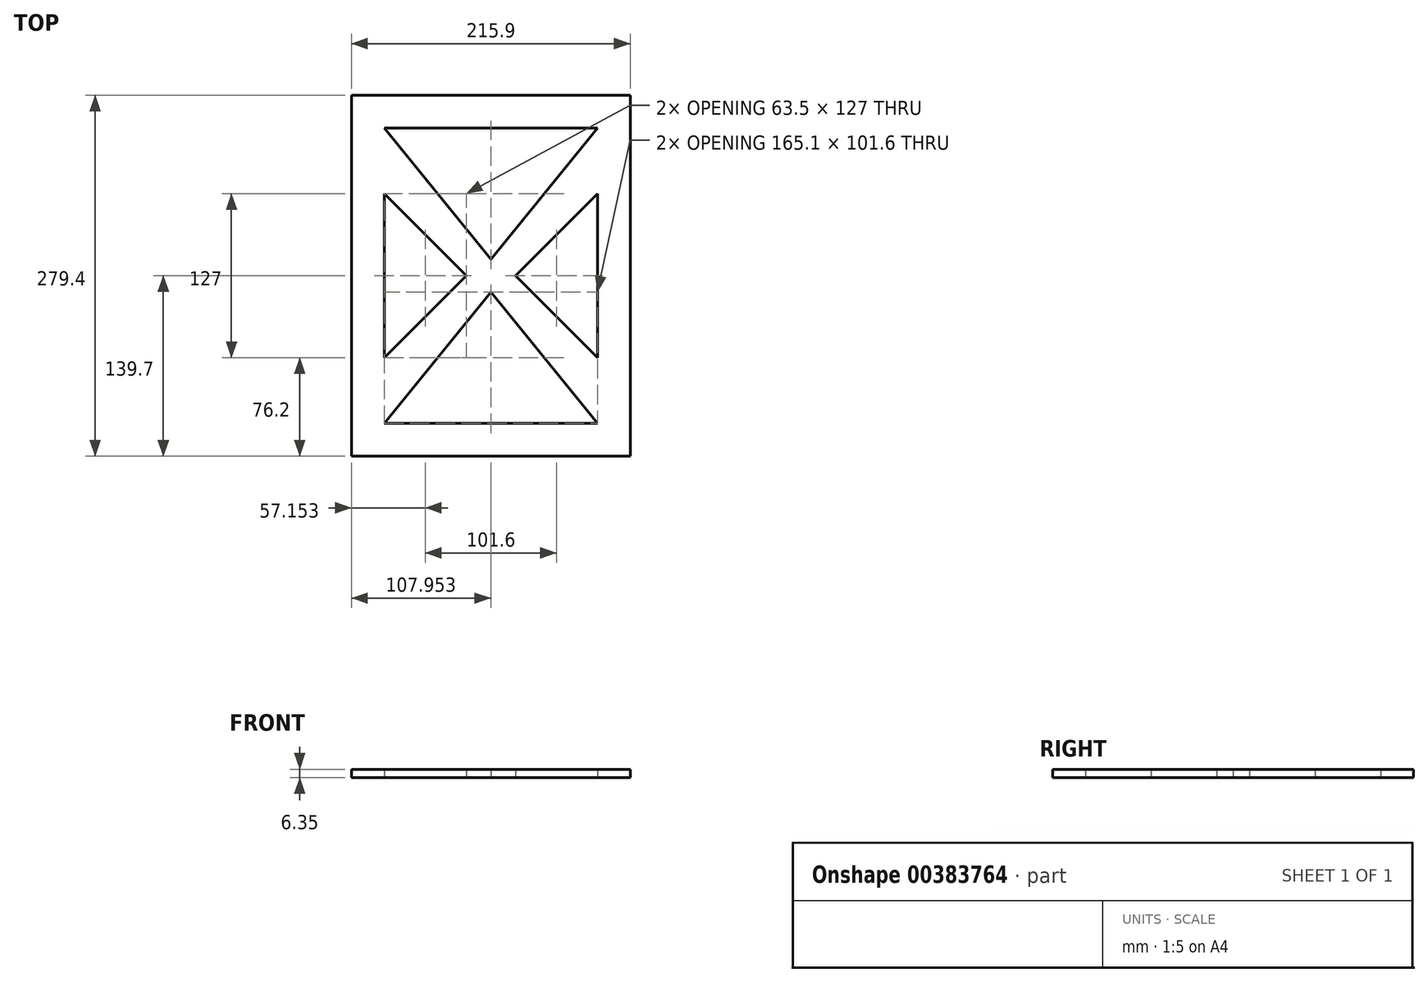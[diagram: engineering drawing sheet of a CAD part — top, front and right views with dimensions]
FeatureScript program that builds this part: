
annotation { "Feature Type Name" : "Feature", "Feature Type Description" : "" }
export const myFeature = defineFeature(function(context is Context, id is Id, definition is map)
    precondition{}
    {
        {
            var Q0;
            Q0=qCreatedBy(makeId("Top.planeOp"),FACE);
            var sketch = newSketch(context, id + "F0", { "sketchPlane" : qUnion([Q0])});
            skLineSegment(sketch, "E0.bottom", {"start": v(4.75, 0) * mm, "end": v(220.65, 0) * mm});
            skLineSegment(sketch, "E0.top", {"start": v(4.75, 279.4) * mm, "end": v(220.65, 279.4) * mm});
            skLineSegment(sketch, "E0.left", {"start": v(4.75, 0) * mm, "end": v(4.75, 279.4) * mm});
            skLineSegment(sketch, "E0.right", {"start": v(220.65, 0) * mm, "end": v(220.65, 279.4) * mm});
            skLineSegment(sketch, "E1.0", {"start": v(30.15, 254) * mm, "end": v(195.25, 254) * mm});
            skLineSegment(sketch, "E2", {"start": v(112.7, 152.4) * mm, "end": v(195.25, 254) * mm});
            skLineSegment(sketch, "E3", {"start": v(112.7, 152.4) * mm, "end": v(30.15, 254) * mm});
            skPoint(sketch, "E4.endSnap0", {"position": v(220.65, 139.7) * mm});
            skLineSegment(sketch, "E5.MirrorCS", {"start": v(112.7, 127) * mm, "end": v(195.25, 25.4) * mm});
            skLineSegment(sketch, "E6.MirrorCS", {"start": v(112.7, 127) * mm, "end": v(30.15, 25.4) * mm});
            skLineSegment(sketch, "E7.MirrorCS", {"start": v(30.15, 25.4) * mm, "end": v(195.25, 25.4) * mm});
            skLineSegment(sketch, "E8", {"start": v(30.15, 203.2) * mm, "end": v(93.65, 139.7) * mm});
            skLineSegment(sketch, "E9", {"start": v(93.65, 139.7) * mm, "end": v(30.15, 76.2) * mm});
            skLineSegment(sketch, "E10.trimOffspring", {"start": v(30.15, 76.2) * mm, "end": v(30.15, 203.2) * mm});
            skLineSegment(sketch, "E11.MirrorCS", {"start": v(131.75, 139.7) * mm, "end": v(195.25, 76.2) * mm});
            skLineSegment(sketch, "E12.MirrorCS", {"start": v(195.25, 76.2) * mm, "end": v(195.25, 203.2) * mm});
            skLineSegment(sketch, "E13.MirrorCS", {"start": v(195.25, 203.2) * mm, "end": v(131.75, 139.7) * mm});
            skSolve(sketch);
        }
        {
            var Q0;
            Q0=makeQuery(id+"F0.imprint","IMPRINT",FACE,{"disambiguationData":[TD([[makeQuery(id+"F0.imprint","IMPRINT",EDGE,{"derivedFrom":sQuery(id+"F0.wireOp",EDGE,"E0.bottom")}),1.0]])]});
            extrude(context, id + "F1", {"entities" : qUnion([Q0]), "depth" : 6.35 * mm});
        }
    });
